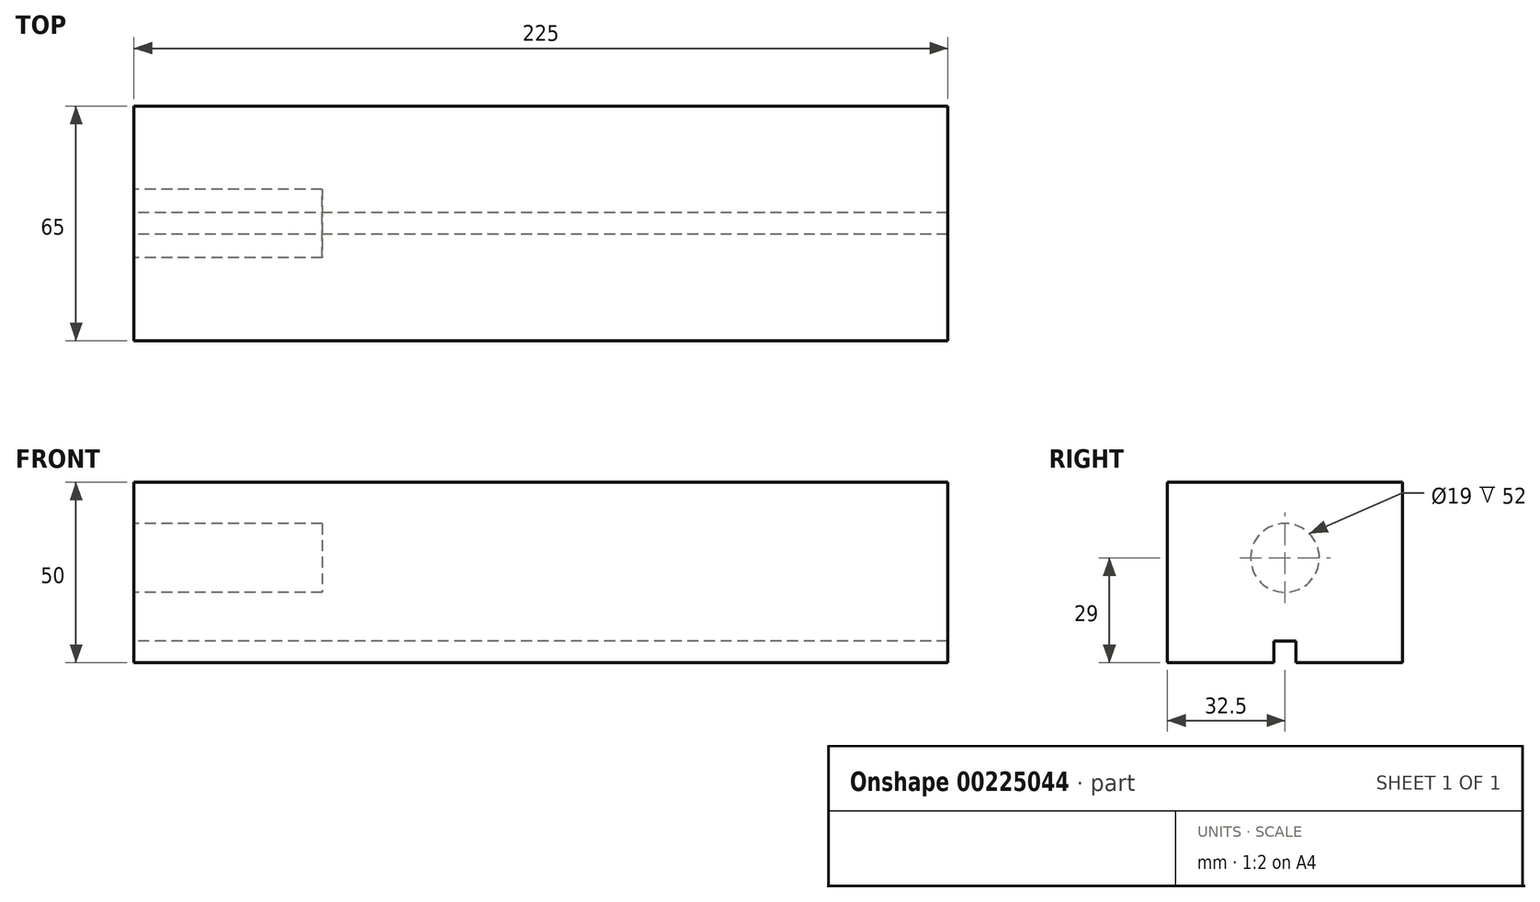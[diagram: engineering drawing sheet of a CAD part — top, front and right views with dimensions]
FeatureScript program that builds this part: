
annotation { "Feature Type Name" : "Feature", "Feature Type Description" : "" }
export const myFeature = defineFeature(function(context is Context, id is Id, definition is map)
    precondition{}
    {
        {
            var Q0;
            Q0=qCreatedBy(makeId("Top.planeOp"),FACE);
            var sketch = newSketch(context, id + "F0", { "sketchPlane" : qUnion([Q0])});
            skLineSegment(sketch, "E0.bottom", {"start": v(112.5, 32.5) * mm, "end": v(-112.5, 32.5) * mm});
            skLineSegment(sketch, "E0.top", {"start": v(112.5, -32.5) * mm, "end": v(-112.5, -32.5) * mm});
            skLineSegment(sketch, "E0.left", {"start": v(112.5, 32.5) * mm, "end": v(112.5, -32.5) * mm});
            skLineSegment(sketch, "E0.right", {"start": v(-112.5, 32.5) * mm, "end": v(-112.5, -32.5) * mm});
            skPoint(sketch, "E0.middle", {"position": v(0, 0) * mm});
            skSolve(sketch);
        }
        {
            var Q0;
            Q0=makeQuery(id+"F0.imprint","IMPRINT",FACE,{"disambiguationData":[TD([[makeQuery(id+"F0.imprint","IMPRINT",EDGE,{"derivedFrom":sQuery(id+"F0.wireOp",EDGE,"E0.bottom")}),1.0]])]});
            extrude(context, id + "F1", {"entities" : qUnion([Q0]), "depth" : 50 * mm});
        }
        {
            var Q0;
            Q0=makeQuery(id+"F1.opExtrude","SWEPT_FACE",FACE,{"disambiguationData":[OSD([sQuery(id+"F0.wireOp",EDGE,"E0.right")])]});
            var sketch = newSketch(context, id + "F2", { "sketchPlane" : qUnion([Q0])});
            skCircle(sketch, "E1", {"center": v(0, 29) * mm, "radius": 9.5 * mm});
            skSolve(sketch);
        }
        {
            var Q0;
            Q0=makeQuery(id+"F2.imprint","IMPRINT",FACE,{"disambiguationData":[TD([[makeQuery(id+"F2.imprint","IMPRINT",EDGE,{"derivedFrom":sQuery(id+"F2.wireOp",EDGE,"E1")}),1.0]])]});
            extrude(context, id + "F3", {"entities" : qUnion([Q0]), "operationType" : NewBodyOperationType.REMOVE, "oppositeDirection" : true, "depth" : 52 * mm});
        }
        {
            var Q0;
            Q0=makeQuery(id+"F1.opExtrude","SWEPT_FACE",FACE,{"disambiguationData":[OSD([sQuery(id+"F0.wireOp",EDGE,"E0.right")])]});
            var sketch = newSketch(context, id + "F4", { "sketchPlane" : qUnion([Q0])});
            skLineSegment(sketch, "E2.bottom", {"start": v(-3, 6) * mm, "end": v(3, 6) * mm});
            skLineSegment(sketch, "E2.top", {"start": v(-3, 0) * mm, "end": v(3, 0) * mm});
            skLineSegment(sketch, "E2.left", {"start": v(-3, 6) * mm, "end": v(-3, 0) * mm});
            skLineSegment(sketch, "E2.right", {"start": v(3, 6) * mm, "end": v(3, 0) * mm});
            skSolve(sketch);
        }
        {
            var Q0;
            Q0=makeQuery(id+"F4.imprint","IMPRINT",FACE,{"disambiguationData":[TD([[makeQuery(id+"F4.imprint","IMPRINT",EDGE,{"derivedFrom":sQuery(id+"F4.wireOp",EDGE,"E2.bottom")}),-1.0]])]});
            extrude(context, id + "F5", {"entities" : qUnion([Q0]), "operationType" : NewBodyOperationType.REMOVE, "oppositeDirection" : true, "depth" : 325 * mm});
        }
    });
